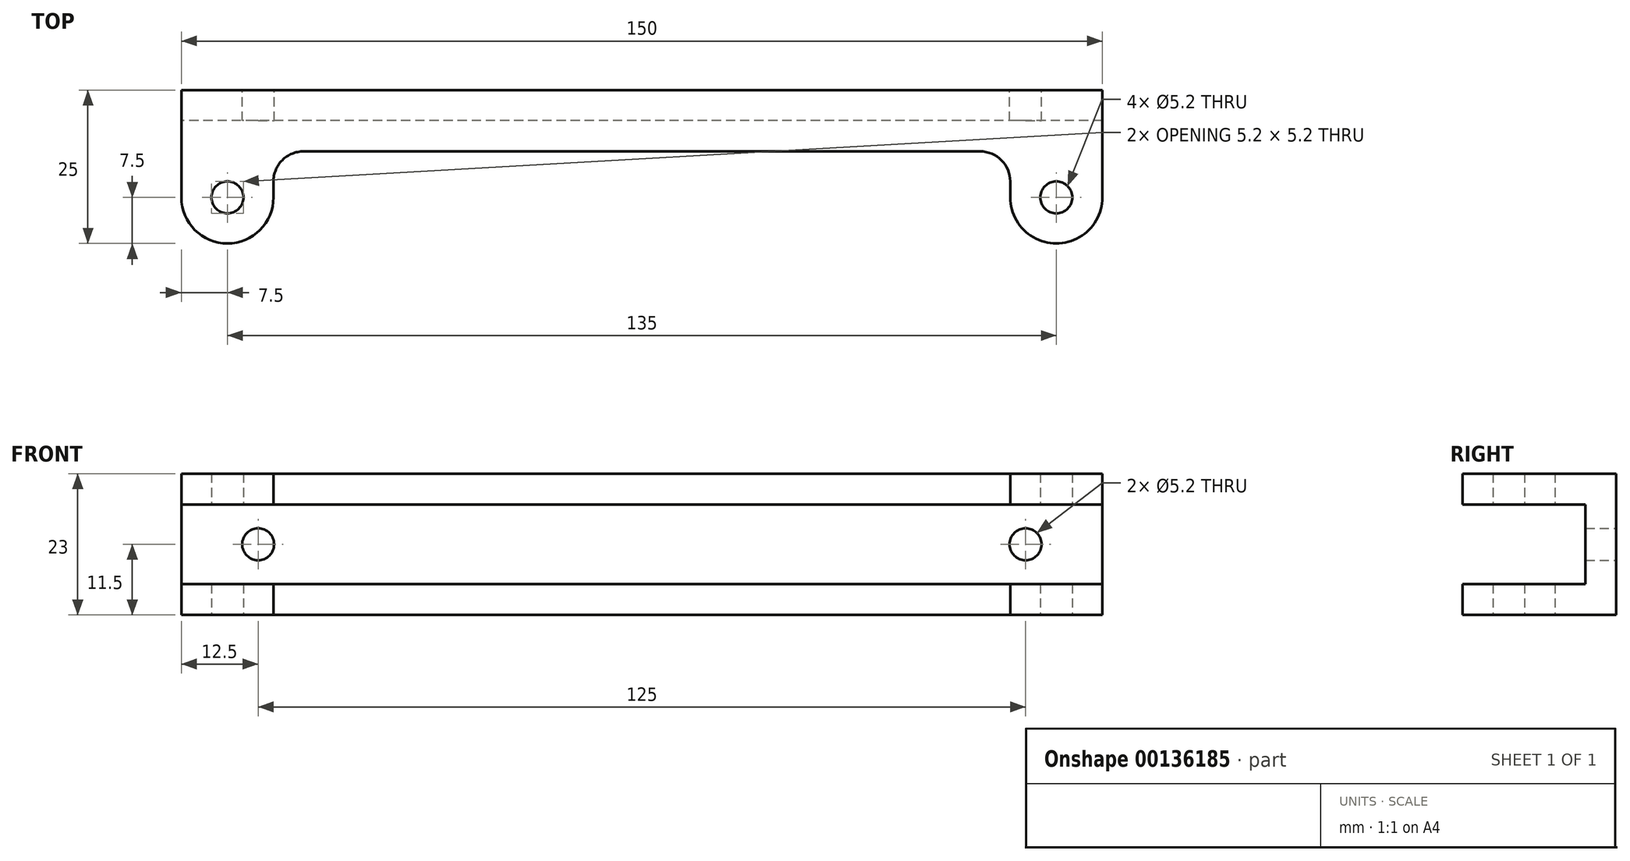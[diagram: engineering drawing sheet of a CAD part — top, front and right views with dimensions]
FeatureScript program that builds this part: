
annotation { "Feature Type Name" : "Feature", "Feature Type Description" : "" }
export const myFeature = defineFeature(function(context is Context, id is Id, definition is map)
    precondition{}
    {
        {
            var Q0;
            Q0=qCreatedBy(makeId("Top.planeOp"),FACE);
            var sketch = newSketch(context, id + "F0", { "sketchPlane" : qUnion([Q0])});
            skLineSegment(sketch, "E0.top", {"start": v(75, 12.5) * mm, "end": v(-75, 12.5) * mm});
            skLineSegment(sketch, "E0.left", {"start": v(75, -5) * mm, "end": v(75, 12.5) * mm});
            skLineSegment(sketch, "E0.right", {"start": v(-75, -5) * mm, "end": v(-75, 12.5) * mm});
            skPoint(sketch, "E0.middle", {"position": v(0, 0) * mm});
            skCircle(sketch, "E1", {"center": v(-67.5, -5) * mm, "radius": 12.5 * mm, "construction": true});
            skArc(sketch, "E2", {"start": v(-75, -5) * mm, "mid": v(-67.5, -12.5) * mm, "end": v(-60, -5) * mm, "construction": true});
            skCircle(sketch, "E3", {"center": v(-67.5, -5) * mm, "radius": 2.6 * mm});
            skCircle(sketch, "E4", {"center": v(67.5, -5) * mm, "radius": 2.6 * mm});
            skArc(sketch, "E5", {"start": v(-75, -5) * mm, "mid": v(-67.5, -12.5) * mm, "end": v(-60, -5) * mm});
            skArc(sketch, "E6", {"start": v(60, -5) * mm, "mid": v(67.5, -12.5) * mm, "end": v(75, -5) * mm});
            skPoint(sketch, "E7.orphan", {"position": v(75, -12.5) * mm});
            skPoint(sketch, "E8.orphan", {"position": v(-75, -12.5) * mm});
            skLineSegment(sketch, "E9", {"start": v(55.1, 2.5) * mm, "end": v(-55.1, 2.5) * mm});
            skLineSegment(sketch, "E10", {"start": v(-60, -5) * mm, "end": v(-60, -2.4) * mm});
            skLineSegment(sketch, "E11", {"start": v(60, -5) * mm, "end": v(60, -2.4) * mm});
            skPoint(sketch, "E12.visualSharp", {"position": v(60, 2.5) * mm});
            skArc(sketch, "E12.filletArc", {"start": v(60, -2.4) * mm, "mid": v(58.56, 1.06) * mm, "end": v(55.1, 2.5) * mm});
            skPoint(sketch, "E13.visualSharp", {"position": v(-60, 2.5) * mm});
            skArc(sketch, "E13.filletArc", {"start": v(-55.1, 2.5) * mm, "mid": v(-58.56, 1.06) * mm, "end": v(-60, -2.4) * mm});
            skSolve(sketch);
        }
        {
            var Q0;
            Q0=makeQuery(id+"F0.imprint","IMPRINT",FACE,{"disambiguationData":[TD([[makeQuery(id+"F0.imprint","IMPRINT",EDGE,{"derivedFrom":sQuery(id+"F0.wireOp",EDGE,"E0.top")}),1.0]])]});
            extrude(context, id + "F1", {"entities" : qUnion([Q0]), "depth" : 23 * mm});
        }
        {
            var Q0;
            Q0=makeQuery(id+"F1.opExtrude","SWEPT_FACE",FACE,{"disambiguationData":[OSD([sQuery(id+"F0.wireOp",EDGE,"E0.right")])]});
            var sketch = newSketch(context, id + "F2", { "sketchPlane" : qUnion([Q0])});
            skLineSegment(sketch, "E14.bottom", {"start": v(-7.5, 5) * mm, "end": v(21.93, 5) * mm});
            skLineSegment(sketch, "E14.top", {"start": v(-7.5, 18) * mm, "end": v(21.93, 18) * mm});
            skLineSegment(sketch, "E14.left", {"start": v(-7.5, 5) * mm, "end": v(-7.5, 18) * mm});
            skLineSegment(sketch, "E14.right", {"start": v(21.93, 5) * mm, "end": v(21.93, 18) * mm});
            skSolve(sketch);
        }
        {
            var Q0;
            {var subQ0=sQuery(id+"F2.wireOp",EDGE,"E14.left");Q0=makeQuery(id+"F2.imprint","IMPRINT",FACE,{"disambiguationData":[TD([[makeQuery(id+"F2.imprint","IMPRINT",EDGE,{"derivedFrom":subQ0}),-1.0]])]});}
            var Q1;
            {var subQ0=sQuery(id+"F2.wireOp",EDGE,"E14.right");Q1=makeQuery(id+"F2.imprint","IMPRINT",FACE,{"disambiguationData":[TD([[makeQuery(id+"F2.imprint","IMPRINT",EDGE,{"derivedFrom":subQ0}),1.0]])]});}
            extrude(context, id + "F3", {"entities" : qUnion([Q0, Q1]), "operationType" : NewBodyOperationType.REMOVE, "endBound" : BoundingType.THROUGH_ALL, "oppositeDirection" : true, "depth" : 25 * mm});
        }
        {
            var Q0;
            Q0=makeQuery(id+"F1.opExtrude","SWEPT_FACE",FACE,{"disambiguationData":[OSD([sQuery(id+"F0.wireOp",EDGE,"E0.top")])]});
            var sketch = newSketch(context, id + "F4", { "sketchPlane" : qUnion([Q0])});
            skLineSegment(sketch, "E15", {"start": v(75, 11.5) * mm, "end": v(-75, 11.5) * mm, "construction": true});
            skCircle(sketch, "E16", {"center": v(62.5, 11.5) * mm, "radius": 2.6 * mm});
            skCircle(sketch, "E17", {"center": v(-62.5, 11.5) * mm, "radius": 2.6 * mm});
            skSolve(sketch);
        }
        {
            var Q0;
            Q0 = qSketchRegion(id + "F4", true);
            extrude(context, id + "F5", {"entities" : qUnion([Q0]), "operationType" : NewBodyOperationType.REMOVE, "endBound" : BoundingType.THROUGH_ALL, "oppositeDirection" : true, "depth" : 25 * mm});
        }
    });
